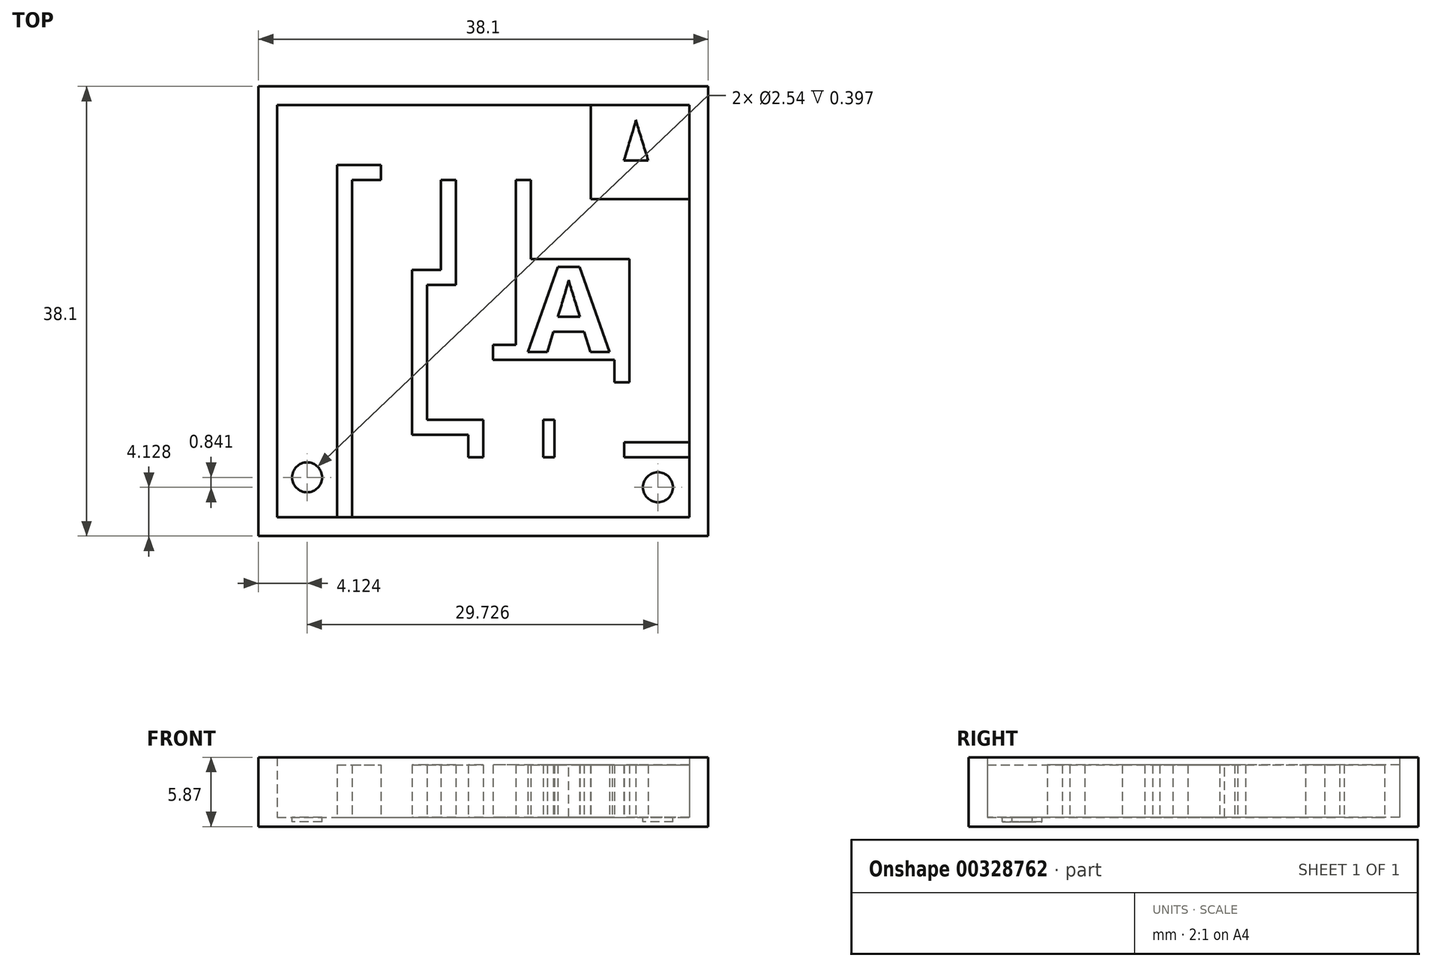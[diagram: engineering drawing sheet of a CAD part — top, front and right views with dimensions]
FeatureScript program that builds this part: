
annotation { "Feature Type Name" : "Feature", "Feature Type Description" : "" }
export const myFeature = defineFeature(function(context is Context, id is Id, definition is map)
    precondition{}
    {
        {
            var Q0;
            Q0=qCreatedBy(makeId("Top.planeOp"),FACE);
            var sketch = newSketch(context, id + "F0", { "sketchPlane" : qUnion([Q0])});
            skLineSegment(sketch, "E0.bottom", {"start": v(-18.81, 16.3) * mm, "end": v(19.29, 16.3) * mm});
            skLineSegment(sketch, "E0.top", {"start": v(-18.81, -21.8) * mm, "end": v(19.29, -21.8) * mm});
            skLineSegment(sketch, "E0.left", {"start": v(-18.81, 16.3) * mm, "end": v(-18.81, -21.8) * mm});
            skLineSegment(sketch, "E0.right", {"start": v(19.29, 16.3) * mm, "end": v(19.29, -21.8) * mm});
            skSolve(sketch);
        }
        {
            var Q0;
            Q0=makeQuery(id+"F0.imprint","IMPRINT",FACE,{"disambiguationData":[TD([[makeQuery(id+"F0.imprint","IMPRINT",EDGE,{"derivedFrom":sQuery(id+"F0.wireOp",EDGE,"E0.bottom")}),-1.0]])]});
            extrude(context, id + "F1", {"entities" : qUnion([Q0]), "depth" : 0.8 * mm});
        }
        {
            var Q0;
            Q0=makeQuery(id+"F1.opExtrude","CAP_FACE",FACE,{"disambiguationData":[OSD([sQuery(id+"F0.wireOp",EDGE,"E0.bottom"),sQuery(id+"F0.wireOp",EDGE,"E0.top"),sQuery(id+"F0.wireOp",EDGE,"E0.left"),sQuery(id+"F0.wireOp",EDGE,"E0.right")])],"isStart":false});
            var sketch = newSketch(context, id + "F2", { "sketchPlane" : qUnion([Q0])});
            skLineSegment(sketch, "E1.0", {"start": v(-17.23, 14.71) * mm, "end": v(17.7, 14.71) * mm});
            skLineSegment(sketch, "E1.1", {"start": v(-17.23, 14.71) * mm, "end": v(-17.23, -20.21) * mm});
            skLineSegment(sketch, "E1.2", {"start": v(-17.23, -20.21) * mm, "end": v(17.7, -20.21) * mm});
            skLineSegment(sketch, "E1.3", {"start": v(17.7, 14.71) * mm, "end": v(17.7, -20.21) * mm});
            skSolve(sketch);
        }
        {
            var Q0;
            Q0=makeQuery(id+"F2.imprint","IMPRINT",FACE,{"disambiguationData":[TD([[makeQuery(id+"F2.imprint","IMPRINT",EDGE,{"derivedFrom":sQuery(id+"F2.wireOp",EDGE,"E1.0")}),1.0]])]});
            extrude(context, id + "F3", {"entities" : qUnion([Q0]), "operationType" : NewBodyOperationType.ADD, "depth" : 5.08 * mm});
        }
        {
            var Q0;
            Q0=makeQuery(id+"F1.opExtrude","CAP_FACE",FACE,{"disambiguationData":[OSD([sQuery(id+"F0.wireOp",EDGE,"E0.bottom"),sQuery(id+"F0.wireOp",EDGE,"E0.top"),sQuery(id+"F0.wireOp",EDGE,"E0.left"),sQuery(id+"F0.wireOp",EDGE,"E0.right")])],"isStart":false});
            var sketch = newSketch(context, id + "F4", { "sketchPlane" : qUnion([Q0])});
            skLineSegment(sketch, "E2.bottom", {"start": v(-12.15, -20.21) * mm, "end": v(-10.88, -20.21) * mm});
            skLineSegment(sketch, "E2.top", {"start": v(-12.15, 9.63) * mm, "end": v(-10.88, 9.63) * mm});
            skLineSegment(sketch, "E2.left", {"start": v(-12.15, -20.21) * mm, "end": v(-12.15, 9.63) * mm});
            skLineSegment(sketch, "E2.right", {"start": v(-10.88, -20.21) * mm, "end": v(-10.88, 8.36) * mm});
            skLineSegment(sketch, "E3.bottom", {"start": v(-10.88, 9.63) * mm, "end": v(-8.43, 9.63) * mm});
            skLineSegment(sketch, "E3.top", {"start": v(-10.88, 8.36) * mm, "end": v(-8.43, 8.36) * mm});
            skLineSegment(sketch, "E3.right", {"start": v(-8.43, 9.63) * mm, "end": v(-8.43, 8.36) * mm});
            skLineSegment(sketch, "E4.bottom", {"start": v(-3.35, 8.36) * mm, "end": v(-2.08, 8.36) * mm});
            skLineSegment(sketch, "E4.left", {"start": v(-3.35, 8.36) * mm, "end": v(-3.35, 0.74) * mm});
            skLineSegment(sketch, "E4.right", {"start": v(-2.08, 8.36) * mm, "end": v(-2.08, 0.74) * mm});
            skLineSegment(sketch, "E5.bottom", {"start": v(3, 8.36) * mm, "end": v(4.27, 8.36) * mm});
            skLineSegment(sketch, "E5.left", {"start": v(3, 8.36) * mm, "end": v(3, 4.37) * mm});
            skLineSegment(sketch, "E5.right", {"start": v(4.27, 8.36) * mm, "end": v(4.27, 0.74) * mm});
            skLineSegment(sketch, "E6.bottom", {"start": v(-3.35, 0.74) * mm, "end": v(-5.8, 0.74) * mm});
            skLineSegment(sketch, "E6.top", {"start": v(-2.08, -0.53) * mm, "end": v(-4.53, -0.53) * mm});
            skLineSegment(sketch, "E6.left", {"start": v(-2.08, 0.74) * mm, "end": v(-2.08, -0.53) * mm});
            skLineSegment(sketch, "E6.right", {"start": v(-5.8, 0.74) * mm, "end": v(-5.8, -0.53) * mm});
            skLineSegment(sketch, "E7.left", {"start": v(4.27, 1.66) * mm, "end": v(4.27, 0.74) * mm});
            skLineSegment(sketch, "E7.right", {"start": v(3, 4.37) * mm, "end": v(3, 1.66) * mm});
            skLineSegment(sketch, "E8.bottom", {"start": v(4.27, 1.66) * mm, "end": v(12.62, 1.66) * mm});
            skLineSegment(sketch, "E8.top", {"start": v(3, -6.88) * mm, "end": v(11.35, -6.88) * mm});
            skLineSegment(sketch, "E8.left", {"start": v(3, 1.66) * mm, "end": v(3, -5.6) * mm});
            skLineSegment(sketch, "E8.right", {"start": v(12.62, 1.66) * mm, "end": v(12.62, -6.88) * mm});
            skLineSegment(sketch, "E9.top", {"start": v(-5.8, -13.23) * mm, "end": v(-4.53, -13.23) * mm});
            skLineSegment(sketch, "E9.left", {"start": v(-5.8, -0.53) * mm, "end": v(-5.8, -13.23) * mm});
            skLineSegment(sketch, "E9.right", {"start": v(-4.53, -0.53) * mm, "end": v(-4.53, -11.96) * mm});
            skLineSegment(sketch, "E10.bottom", {"start": v(3, -5.6) * mm, "end": v(1.06, -5.6) * mm});
            skLineSegment(sketch, "E10.top", {"start": v(6.27, -6.88) * mm, "end": v(1.06, -6.88) * mm});
            skLineSegment(sketch, "E10.right", {"start": v(1.06, -5.6) * mm, "end": v(1.06, -6.88) * mm});
            skLineSegment(sketch, "E11.bottom", {"start": v(-4.53, -11.96) * mm, "end": v(0.23, -11.96) * mm});
            skLineSegment(sketch, "E11.top", {"start": v(-4.53, -13.23) * mm, "end": v(-1.04, -13.23) * mm});
            skLineSegment(sketch, "E11.right", {"start": v(0.23, -11.96) * mm, "end": v(0.23, -13.23) * mm});
            skLineSegment(sketch, "E12.top", {"start": v(0.23, -15.13) * mm, "end": v(-1.04, -15.13) * mm});
            skLineSegment(sketch, "E12.left", {"start": v(0.23, -13.23) * mm, "end": v(0.23, -15.13) * mm});
            skLineSegment(sketch, "E12.right", {"start": v(-1.04, -13.23) * mm, "end": v(-1.04, -15.13) * mm});
            skLineSegment(sketch, "E13.top", {"start": v(11.35, -8.78) * mm, "end": v(12.62, -8.78) * mm});
            skLineSegment(sketch, "E13.left", {"start": v(11.35, -6.88) * mm, "end": v(11.35, -8.78) * mm});
            skLineSegment(sketch, "E13.right", {"start": v(12.62, -6.85) * mm, "end": v(12.62, -8.78) * mm});
            skLineSegment(sketch, "E14.bottom", {"start": v(5.31, -11.96) * mm, "end": v(6.27, -11.96) * mm});
            skLineSegment(sketch, "E14.top", {"start": v(5.31, -15.13) * mm, "end": v(6.27, -15.13) * mm});
            skLineSegment(sketch, "E14.left", {"start": v(5.31, -11.96) * mm, "end": v(5.31, -15.13) * mm});
            skLineSegment(sketch, "E14.right", {"start": v(6.27, -11.96) * mm, "end": v(6.27, -15.13) * mm});
            skLineSegment(sketch, "E15.bottom", {"start": v(17.7, -13.86) * mm, "end": v(12.16, -13.86) * mm});
            skLineSegment(sketch, "E15.top", {"start": v(17.7, -15.13) * mm, "end": v(12.16, -15.13) * mm});
            skLineSegment(sketch, "E15.left", {"start": v(17.7, -13.86) * mm, "end": v(17.7, -15.13) * mm});
            skLineSegment(sketch, "E15.right", {"start": v(12.16, -13.86) * mm, "end": v(12.16, -15.13) * mm});
            skLineSegment(sketch, "E16.bottom", {"start": v(9.35, 14.71) * mm, "end": v(17.7, 14.71) * mm});
            skLineSegment(sketch, "E16.top", {"start": v(9.35, 6.74) * mm, "end": v(17.7, 6.74) * mm});
            skLineSegment(sketch, "E16.left", {"start": v(9.35, 14.71) * mm, "end": v(9.35, 6.74) * mm});
            skLineSegment(sketch, "E16.right", {"start": v(17.7, 14.71) * mm, "end": v(17.7, 6.74) * mm});
            skText(sketch, "E17", { "text": "A", "fontName": "OpenSans-Bold.ttf"});
            const initialGuessF4  = {"E17": [0.00935, 0.00674, 1, 0, 0.00797]};
            skSetInitialGuess(sketch, initialGuessF4);
            skSolve(sketch);
        }
        {
            var Q0;
            Q0 = qSketchRegion(id + "F4", true);
            extrude(context, id + "F5", {"entities" : qUnion([Q0]), "operationType" : NewBodyOperationType.ADD, "depth" : 4.44 * mm});
        }
        {
            var Q0;
            Q0=makeQuery(id+"F1.opExtrude","CAP_FACE",FACE,{"disambiguationData":[OSD([sQuery(id+"F0.wireOp",EDGE,"E0.bottom"),sQuery(id+"F0.wireOp",EDGE,"E0.top"),sQuery(id+"F0.wireOp",EDGE,"E0.left"),sQuery(id+"F0.wireOp",EDGE,"E0.right")])],"isStart":false});
            var sketch = newSketch(context, id + "F6", { "sketchPlane" : qUnion([Q0])});
            skLineSegment(sketch, "E18", {"start": v(-17.23, -20.21) * mm, "end": v(-12.15, -20.21) * mm});
            skCircle(sketch, "E19", {"center": v(-14.69, -16.83) * mm, "radius": 1.27 * mm});
            skPoint(sketch, "E19.centerSnap0", {"position": v(-14.69, -20.21) * mm});
            skCircle(sketch, "E20", {"center": v(15.04, -17.67) * mm, "radius": 1.27 * mm});
            skPoint(sketch, "E20.centerSnap0", {"position": v(17.7, -17.67) * mm});
            skText(sketch, "E21", { "text": "A", "fontName": "OpenSans-Bold.ttf"});
            const initialGuessF6  = {"E21": [0.00401, -0.00621, 1, 0, 0.00724]};
            skSetInitialGuess(sketch, initialGuessF6);
            skSolve(sketch);
        }
        {
            var Q0;
            Q0=makeQuery(id+"F4.imprint","IMPRINT",FACE,{"disambiguationData":[TD([[makeQuery(id+"F4.imprint","IMPRINT",EDGE,{"derivedFrom":sQuery(id+"F4.wireOp",EDGE,"E17.sketch_text.stroke-0")}),-1.0]])]});
            extrude(context, id + "F7", {"entities" : qUnion([Q0]), "operationType" : NewBodyOperationType.REMOVE, "depth" : 25.4 * mm});
        }
        {
            var Q0;
            Q0 = qSketchRegion(id + "F6", true);
            var Q1;
            Q1=makeQuery(id+"F6.imprint","IMPRINT",FACE,{"disambiguationData":[TD([[makeQuery(id+"F6.imprint","IMPRINT",EDGE,{"derivedFrom":makeQuery(id+"F5.opExtrude","CAP_EDGE",EDGE,{"disambiguationData":[OSD([sQuery(id+"F4.wireOp",EDGE,"E17.sketch_text.stroke-8")])],"isStart":true})}),1.0]])]});
            extrude(context, id + "F8", {"entities" : qUnion([Q0, Q1]), "operationType" : NewBodyOperationType.ADD, "depth" : 4.44 * mm});
        }
        {
            var Q0;
            Q0 = qSketchRegion(id + "F6", true);
            extrude(context, id + "F9", {"entities" : qUnion([Q0]), "operationType" : NewBodyOperationType.REMOVE, "depth" : 4.44 * mm});
        }
        {
            var Q0;
            Q0=makeQuery(id+"F6.imprint","IMPRINT",FACE,{"disambiguationData":[TD([[makeQuery(id+"F6.imprint","IMPRINT",EDGE,{"derivedFrom":sQuery(id+"F6.wireOp",EDGE,"E19")}),1.0]])]});
            extrude(context, id + "F10", {"entities" : qUnion([Q0]), "operationType" : NewBodyOperationType.REMOVE, "oppositeDirection" : true, "depth" : 0.4 * mm});
        }
        {
            var Q0;
            Q0=makeQuery(id+"F6.imprint","IMPRINT",FACE,{"disambiguationData":[TD([[makeQuery(id+"F6.imprint","IMPRINT",EDGE,{"derivedFrom":sQuery(id+"F6.wireOp",EDGE,"E20")}),1.0]])]});
            extrude(context, id + "F11", {"entities" : qUnion([Q0]), "operationType" : NewBodyOperationType.REMOVE, "oppositeDirection" : true, "depth" : 0.4 * mm});
        }
    });
